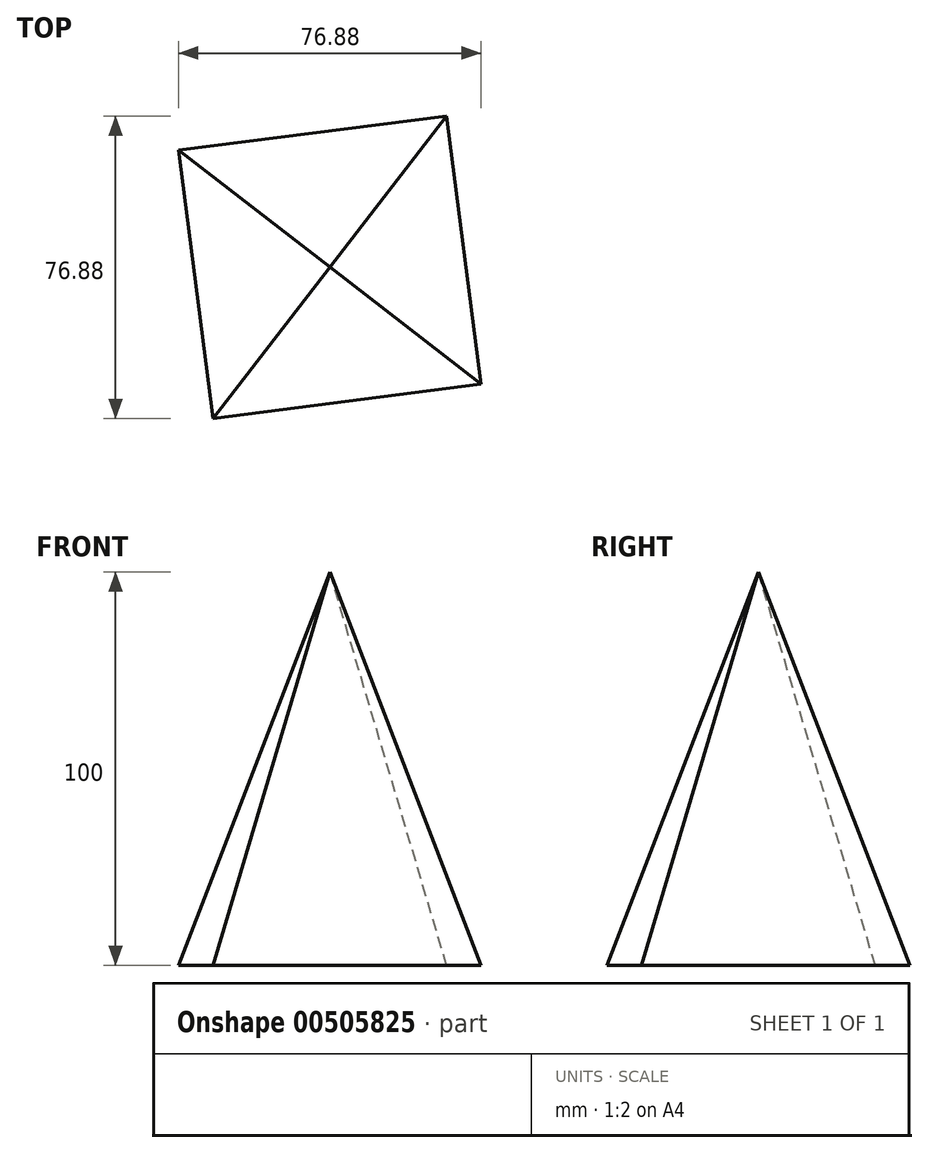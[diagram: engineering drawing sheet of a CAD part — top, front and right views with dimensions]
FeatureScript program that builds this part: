
annotation { "Feature Type Name" : "Feature", "Feature Type Description" : "" }
export const myFeature = defineFeature(function(context is Context, id is Id, definition is map)
    precondition{}
    {
        {
            var Q0;
            Q0=qCreatedBy(makeId("Top.planeOp"),FACE);
            var sketch = newSketch(context, id + "F0", { "sketchPlane" : qUnion([Q0])});
            skCircle(sketch, "E0.cCircle", {"center": v(0, 0) * mm, "radius": 48.57 * mm, "construction": true});
            skLineSegment(sketch, "E0.0", {"start": v(-38.44, 29.7) * mm, "end": v(29.7, 38.44) * mm});
            skLineSegment(sketch, "E0.1", {"start": v(29.7, 38.44) * mm, "end": v(38.44, -29.7) * mm});
            skLineSegment(sketch, "E0.2", {"start": v(38.44, -29.7) * mm, "end": v(-29.7, -38.44) * mm});
            skLineSegment(sketch, "E0.3", {"start": v(-29.7, -38.44) * mm, "end": v(-38.44, 29.7) * mm});
            skSolve(sketch);
        }
        {
            var Q0;
            Q0=qCreatedBy(makeId("Top.planeOp"),FACE);
            cPlane(context, id + "F1", {"entities" : qUnion([Q0]), "cplaneType" : CPlaneType.OFFSET, "offset" : 100 * mm, "width" : 150 * mm, "height" : 150 * mm});
        }
        {
            var Q0;
            Q0=qCreatedBy(id+"F1.planeOp",FACE);
            var sketch = newSketch(context, id + "F2", { "sketchPlane" : qUnion([Q0])});
            skPoint(sketch, "E1", {"position": v(0, 0) * mm});
            skSolve(sketch);
        }
        {
            var Q0;
            Q0=makeQuery(id+"F0.imprint","IMPRINT",FACE,{"disambiguationData":[TD([[makeQuery(id+"F0.imprint","IMPRINT",EDGE,{"derivedFrom":sQuery(id+"F0.wireOp",EDGE,"E0.0")}),-1.0]])]});
            var Q1;
            Q1=sQuery(id+"F2.wireOp",VERTEX,"E1");
            loft(context, id + "F3", {"sheetProfilesArray" : [{ "sheetProfileEntities" : qUnion([Q0]) }, { "sheetProfileEntities" : qUnion([Q1]) }]});
        }
    });
